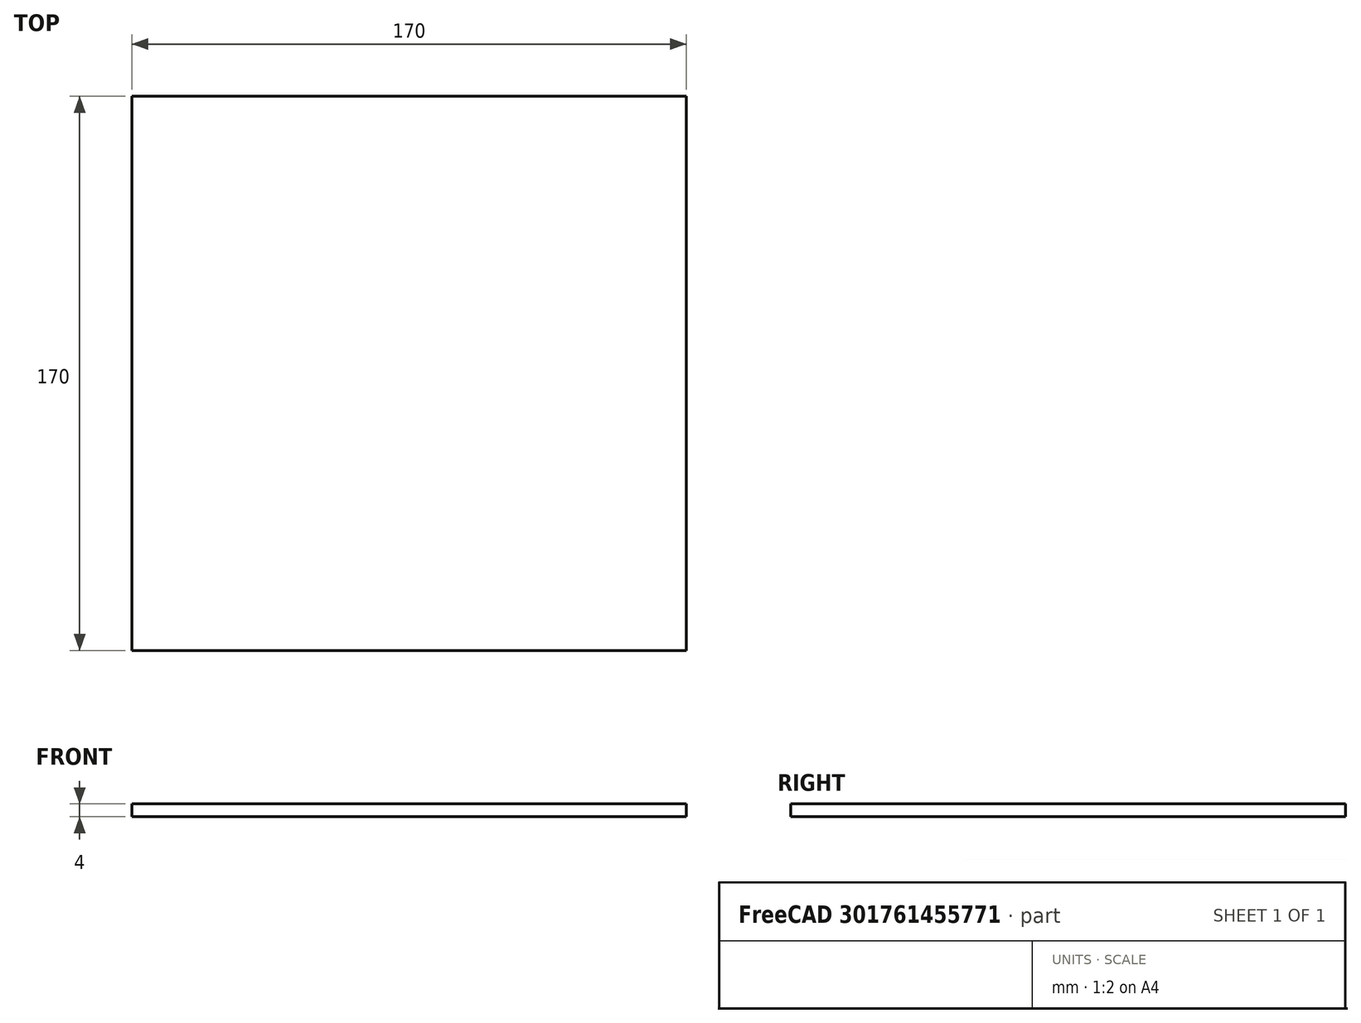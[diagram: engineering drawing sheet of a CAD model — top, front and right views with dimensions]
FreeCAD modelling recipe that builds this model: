
FCSTD DOCUMENT  (FreeCAD 1.0R39319 (Git))
Label: newAttempt
License: All rights reserved
LicenseURL: https://en.wikipedia.org/wiki/All_rights_reserved
objects: Sketcher::SketchObject×2, PartDesign::Pad×1, PartDesign::Body×1
note: 8 computed .brp shape members not serialized (recipe doc carries the construction recipe); baked Part::Feature solids carry a one-line shape summary decoded from their .brp

FEATURE [Sketcher::SketchObject] Sketch
  ArcFitTolerance = 1e-06
  AttachmentSupport = -> [XY_Plane]
  FullyConstrained = true
  MakeInternals = false
  MapMode = 5
  sketch-geometry (4):
    g0: LineSegment StartX=-85 StartY=85 StartZ=0 EndX=-85 EndY=-85 EndZ=0
    g1: LineSegment StartX=-85 StartY=-85 StartZ=0 EndX=85 EndY=-85 EndZ=0
    g2: LineSegment StartX=85 StartY=-85 StartZ=0 EndX=85 EndY=85 EndZ=0
    g3: LineSegment StartX=85 StartY=85 StartZ=0 EndX=-85 EndY=85 EndZ=0
  constraints (12):
    c: Coincident(g0,g1)
    c: Coincident(g1,g2)
    c: Coincident(g2,g3)
    c: Coincident(g3,g0)
    c: Vertical(g0)
    c: Vertical(g2)
    c: Horizontal(g1)
    c: Horizontal(g3)
    c: Distance(g0,g2) = 170
    c: Distance(g1,g3) = 170
    c: Distance(g-1,g3) = 85
    c: Distance(g0,g-2) = 85
FEATURE [PartDesign::Pad] Pad
  Direction = (0,0,1)
  Length = 4
  Length2 = 10
  Profile = -> Sketch
  ReferenceAxis = -> Sketch [N_Axis]
  Refine = true
  Suppressed = false
  Type = 0
FEATURE [Sketcher::SketchObject] Sketch001
  ArcFitTolerance = 1e-06
  AttachmentSupport = -> [Pad]
  FullyConstrained = false
  MakeInternals = false
  MapMode = 5
  Placement = pos=(0,0,4) rot=(0,0,1;0rad)
  sketch-geometry (96):
    g0: LineSegment StartX=-68.03 StartY=63 StartZ=0 EndX=-68.03 EndY=60.51 EndZ=0
    g1: LineSegment StartX=-68.03 StartY=60.51 StartZ=0 EndX=-57.97 EndY=60.51 EndZ=0
    g2: LineSegment StartX=-57.97 StartY=60.51 StartZ=0 EndX=-57.97 EndY=65.54 EndZ=0
    g3: LineSegment StartX=-57.97 StartY=65.54 StartZ=0 EndX=-63 EndY=65.54 EndZ=0
    g4: LineSegment StartX=-63 StartY=65.54 StartZ=0 EndX=-63 EndY=63 EndZ=0
    g5: LineSegment StartX=-63 StartY=63 StartZ=0 EndX=-68.03 EndY=63 EndZ=0
    g6: LineSegment StartX=-26.03 StartY=63 StartZ=0 EndX=-26.03 EndY=60.51 EndZ=0
    g7: LineSegment StartX=-26.03 StartY=60.51 StartZ=0 EndX=-15.97 EndY=60.51 EndZ=0
    g8: LineSegment StartX=-15.97 StartY=60.51 StartZ=0 EndX=-15.97 EndY=65.54 EndZ=0
    g9: LineSegment StartX=-15.97 StartY=65.54 StartZ=0 EndX=-21 EndY=65.54 EndZ=0
    g10: LineSegment StartX=-21 StartY=65.54 StartZ=0 EndX=-21 EndY=63 EndZ=0
    g11: LineSegment StartX=-21 StartY=63 StartZ=0 EndX=-26.03 EndY=63 EndZ=0
    g12: LineSegment StartX=15.97 StartY=63 StartZ=0 EndX=15.97 EndY=60.51 EndZ=0
    g13: LineSegment StartX=15.97 StartY=60.51 StartZ=0 EndX=26.03 EndY=60.51 EndZ=0
    g14: LineSegment StartX=26.03 StartY=60.51 StartZ=0 EndX=26.03 EndY=65.54 EndZ=0
    g15: LineSegment StartX=26.03 StartY=65.54 StartZ=0 EndX=21 EndY=65.54 EndZ=0
    g16: LineSegment StartX=21 StartY=65.54 StartZ=0 EndX=21 EndY=63 EndZ=0
    g17: LineSegment StartX=21 StartY=63 StartZ=0 EndX=15.97 EndY=63 EndZ=0
    g18: LineSegment StartX=57.97 StartY=63 StartZ=0 EndX=57.97 EndY=60.51 EndZ=0
    g19: LineSegment StartX=57.97 StartY=60.51 StartZ=0 EndX=68.03 EndY=60.51 EndZ=0
    g20: LineSegment StartX=68.03 StartY=60.51 StartZ=0 EndX=68.03 EndY=65.54 EndZ=0
    g21: LineSegment StartX=68.03 StartY=65.54 StartZ=0 EndX=63 EndY=65.54 EndZ=0
    g22: LineSegment StartX=63 StartY=65.54 StartZ=0 EndX=63 EndY=63 EndZ=0
    g23: LineSegment StartX=63 StartY=63 StartZ=0 EndX=57.97 EndY=63 EndZ=0
    g24: LineSegment StartX=-68.03 StartY=21 StartZ=0 EndX=-68.03 EndY=18.51 EndZ=0
    g25: LineSegment StartX=-68.03 StartY=18.51 StartZ=0 EndX=-57.97 EndY=18.51 EndZ=0
    g26: LineSegment StartX=-57.97 StartY=18.51 StartZ=0 EndX=-57.97 EndY=23.54 EndZ=0
    g27: LineSegment StartX=-57.97 StartY=23.54 StartZ=0 EndX=-63 EndY=23.54 EndZ=0
    g28: LineSegment StartX=-63 StartY=23.54 StartZ=0 EndX=-63 EndY=21 EndZ=0
    g29: LineSegment StartX=-63 StartY=21 StartZ=0 EndX=-68.03 EndY=21 EndZ=0
    g30: LineSegment StartX=-26.03 StartY=21 StartZ=0 EndX=-26.03 EndY=18.51 EndZ=0
    g31: LineSegment StartX=-26.03 StartY=18.51 StartZ=0 EndX=-15.97 EndY=18.51 EndZ=0
    g32: LineSegment StartX=-15.97 StartY=18.51 StartZ=0 EndX=-15.97 EndY=23.54 EndZ=0
    g33: LineSegment StartX=-15.97 StartY=23.54 StartZ=0 EndX=-21 EndY=23.54 EndZ=0
    g34: LineSegment StartX=-21 StartY=23.54 StartZ=0 EndX=-21 EndY=21 EndZ=0
    g35: LineSegment StartX=-21 StartY=21 StartZ=0 EndX=-26.03 EndY=21 EndZ=0
    g36: LineSegment StartX=15.97 StartY=21 StartZ=0 EndX=15.97 EndY=18.51 EndZ=0
    g37: LineSegment StartX=15.97 StartY=18.51 StartZ=0 EndX=26.03 EndY=18.51 EndZ=0
    g38: LineSegment StartX=26.03 StartY=18.51 StartZ=0 EndX=26.03 EndY=23.54 EndZ=0
    g39: LineSegment StartX=26.03 StartY=23.54 StartZ=0 EndX=21 EndY=23.54 EndZ=0
    g40: LineSegment StartX=21 StartY=23.54 StartZ=0 EndX=21 EndY=21 EndZ=0
    g41: LineSegment StartX=21 StartY=21 StartZ=0 EndX=15.97 EndY=21 EndZ=0
    g42: LineSegment StartX=57.97 StartY=21 StartZ=0 EndX=57.97 EndY=18.51 EndZ=0
    g43: LineSegment StartX=57.97 StartY=18.51 StartZ=0 EndX=68.03 EndY=18.51 EndZ=0
    g44: LineSegment StartX=68.03 StartY=18.51 StartZ=0 EndX=68.03 EndY=23.54 EndZ=0
    g45: LineSegment StartX=68.03 StartY=23.54 StartZ=0 EndX=63 EndY=23.54 EndZ=0
    g46: LineSegment StartX=63 StartY=23.54 StartZ=0 EndX=63 EndY=21 EndZ=0
    g47: LineSegment StartX=63 StartY=21 StartZ=0 EndX=57.97 EndY=21 EndZ=0
    g48: LineSegment StartX=-68.03 StartY=-21 StartZ=0 EndX=-68.03 EndY=-23.49 EndZ=0
    g49: LineSegment StartX=-68.03 StartY=-23.49 StartZ=0 EndX=-57.97 EndY=-23.49 EndZ=0
    g50: LineSegment StartX=-57.97 StartY=-23.49 StartZ=0 EndX=-57.97 EndY=-18.46 EndZ=0
    g51: LineSegment StartX=-57.97 StartY=-18.46 StartZ=0 EndX=-63 EndY=-18.46 EndZ=0
    g52: LineSegment StartX=-63 StartY=-18.46 StartZ=0 EndX=-63 EndY=-21 EndZ=0
    g53: LineSegment StartX=-63 StartY=-21 StartZ=0 EndX=-68.03 EndY=-21 EndZ=0
    g54: LineSegment StartX=-26.03 StartY=-21 StartZ=0 EndX=-26.03 EndY=-23.49 EndZ=0
    g55: LineSegment StartX=-26.03 StartY=-23.49 StartZ=0 EndX=-15.97 EndY=-23.49 EndZ=0
    g56: LineSegment StartX=-15.97 StartY=-23.49 StartZ=0 EndX=-15.97 EndY=-18.46 EndZ=0
    g57: LineSegment StartX=-15.97 StartY=-18.46 StartZ=0 EndX=-21 EndY=-18.46 EndZ=0
    g58: LineSegment StartX=-21 StartY=-18.46 StartZ=0 EndX=-21 EndY=-21 EndZ=0
    g59: LineSegment StartX=-21 StartY=-21 StartZ=0 EndX=-26.03 EndY=-21 EndZ=0
    g60: LineSegment StartX=15.97 StartY=-21 StartZ=0 EndX=15.97 EndY=-23.49 EndZ=0
    g61: LineSegment StartX=15.97 StartY=-23.49 StartZ=0 EndX=26.03 EndY=-23.49 EndZ=0
    g62: LineSegment StartX=26.03 StartY=-23.49 StartZ=0 EndX=26.03 EndY=-18.46 EndZ=0
    g63: LineSegment StartX=26.03 StartY=-18.46 StartZ=0 EndX=21 EndY=-18.46 EndZ=0
    g64: LineSegment StartX=21 StartY=-18.46 StartZ=0 EndX=21 EndY=-21 EndZ=0
    g65: LineSegment StartX=21 StartY=-21 StartZ=0 EndX=15.97 EndY=-21 EndZ=0
    g66: LineSegment StartX=57.97 StartY=-21 StartZ=0 EndX=57.97 EndY=-23.49 EndZ=0
    g67: LineSegment StartX=57.97 StartY=-23.49 StartZ=0 EndX=68.03 EndY=-23.49 EndZ=0
    g68: LineSegment StartX=68.03 StartY=-23.49 StartZ=0 EndX=68.03 EndY=-18.46 EndZ=0
    g69: LineSegment StartX=68.03 StartY=-18.46 StartZ=0 EndX=63 EndY=-18.46 EndZ=0
    g70: LineSegment StartX=63 StartY=-18.46 StartZ=0 EndX=63 EndY=-21 EndZ=0
    g71: LineSegment StartX=63 StartY=-21 StartZ=0 EndX=57.97 EndY=-21 EndZ=0
    g72: LineSegment StartX=-68.03 StartY=-63 StartZ=0 EndX=-68.03 EndY=-65.49 EndZ=0
    g73: LineSegment StartX=-68.03 StartY=-65.49 StartZ=0 EndX=-57.97 EndY=-65.49 EndZ=0
    g74: LineSegment StartX=-57.97 StartY=-65.49 StartZ=0 EndX=-57.97 EndY=-60.46 EndZ=0
    g75: LineSegment StartX=-57.97 StartY=-60.46 StartZ=0 EndX=-63 EndY=-60.46 EndZ=0
    g76: LineSegment StartX=-63 StartY=-60.46 StartZ=0 EndX=-63 EndY=-63 EndZ=0
    g77: LineSegment StartX=-63 StartY=-63 StartZ=0 EndX=-68.03 EndY=-63 EndZ=0
    g78: LineSegment StartX=-26.03 StartY=-63 StartZ=0 EndX=-26.03 EndY=-65.49 EndZ=0
    g79: LineSegment StartX=-26.03 StartY=-65.49 StartZ=0 EndX=-15.97 EndY=-65.49 EndZ=0
    g80: LineSegment StartX=-15.97 StartY=-65.49 StartZ=0 EndX=-15.97 EndY=-60.46 EndZ=0
    g81: LineSegment StartX=-15.97 StartY=-60.46 StartZ=0 EndX=-21 EndY=-60.46 EndZ=0
    g82: LineSegment StartX=-21 StartY=-60.46 StartZ=0 EndX=-21 EndY=-63 EndZ=0
    g83: LineSegment StartX=-21 StartY=-63 StartZ=0 EndX=-26.03 EndY=-63 EndZ=0
    g84: LineSegment StartX=15.97 StartY=-63 StartZ=0 EndX=15.97 EndY=-65.49 EndZ=0
    g85: LineSegment StartX=15.97 StartY=-65.49 StartZ=0 EndX=26.03 EndY=-65.49 EndZ=0
    g86: LineSegment StartX=26.03 StartY=-65.49 StartZ=0 EndX=26.03 EndY=-60.46 EndZ=0
    g87: LineSegment StartX=26.03 StartY=-60.46 StartZ=0 EndX=21 EndY=-60.46 EndZ=0
    g88: LineSegment StartX=21 StartY=-60.46 StartZ=0 EndX=21 EndY=-63 EndZ=0
    g89: LineSegment StartX=21 StartY=-63 StartZ=0 EndX=15.97 EndY=-63 EndZ=0
    g90: LineSegment StartX=57.97 StartY=-63 StartZ=0 EndX=57.97 EndY=-65.49 EndZ=0
    g91: LineSegment StartX=57.97 StartY=-65.49 StartZ=0 EndX=68.03 EndY=-65.49 EndZ=0
    g92: LineSegment StartX=68.03 StartY=-65.49 StartZ=0 EndX=68.03 EndY=-60.46 EndZ=0
    g93: LineSegment StartX=68.03 StartY=-60.46 StartZ=0 EndX=63 EndY=-60.46 EndZ=0
    g94: LineSegment StartX=63 StartY=-60.46 StartZ=0 EndX=63 EndY=-63 EndZ=0
    g95: LineSegment StartX=63 StartY=-63 StartZ=0 EndX=57.97 EndY=-63 EndZ=0
  constraints (268):
    c: Vertical(g0)
    c: Coincident(g0,g1)
    c: Horizontal(g1)
    c: Coincident(g1,g2)
    c: Vertical(g2)
    c: Coincident(g2,g3)
    c: Horizontal(g3)
    c: Coincident(g3,g4)
    c: Vertical(g4)
    c: Coincident(g4,g5)
    c: Coincident(g5,g0)
    c: Perpendicular(g4,g5)
    c: DistanceX(g3,g3) = 5.03
    c: Equal(g3,g5)
    c: Equal(g3,g2)
    c: DistanceY(g0,g0) = 2.49
    c: Distance(g4,g-2) = 63
    c: Distance(g4,g-1) = 63
    c: Vertical(g6)
    c: Vertical(g12)
    c: Vertical(g18)
    c: Vertical(g24)
    c: Vertical(g30)
    c: Vertical(g36)
    c: Vertical(g42)
    c: Vertical(g48)
    c: Vertical(g54)
    c: Vertical(g60)
    c: Vertical(g66)
    c: Vertical(g72)
    c: Vertical(g78)
    c: Vertical(g84)
    c: Vertical(g90)
    c: Coincident(g6,g7)
    c: Coincident(g12,g13)
    c: Coincident(g18,g19)
    c: Coincident(g24,g25)
    c: Coincident(g30,g31)
    c: Coincident(g36,g37)
    c: Coincident(g42,g43)
    c: Coincident(g48,g49)
    c: Coincident(g54,g55)
    c: Coincident(g60,g61)
    c: Coincident(g66,g67)
    c: Coincident(g72,g73)
    c: Coincident(g78,g79)
    c: Coincident(g84,g85)
    c: Coincident(g90,g91)
    c: Horizontal(g7)
    c: Horizontal(g13)
    c: Horizontal(g19)
    c: Horizontal(g25)
    c: Horizontal(g31)
    c: Horizontal(g37)
    c: Horizontal(g43)
    c: Horizontal(g49)
    c: Horizontal(g55)
    c: Horizontal(g61)
    c: Horizontal(g67)
    c: Horizontal(g73)
    c: Horizontal(g79)
    c: Horizontal(g85)
    c: Horizontal(g91)
    c: Coincident(g7,g8)
    c: Coincident(g13,g14)
    c: Coincident(g19,g20)
    c: Coincident(g25,g26)
    c: Coincident(g31,g32)
    c: Coincident(g37,g38)
    c: Coincident(g43,g44)
    c: Coincident(g49,g50)
    c: Coincident(g55,g56)
    c: Coincident(g61,g62)
    c: Coincident(g67,g68)
    c: Coincident(g73,g74)
    c: Coincident(g79,g80)
    c: Coincident(g85,g86)
    c: Coincident(g91,g92)
    c: Vertical(g8)
    c: Vertical(g14)
    c: Vertical(g20)
    c: Vertical(g26)
    c: Vertical(g32)
    c: Vertical(g38)
    c: Vertical(g44)
    c: Vertical(g50)
    c: Vertical(g56)
    c: Vertical(g62)
    c: Vertical(g68)
    c: Vertical(g74)
    c: Vertical(g80)
    c: Vertical(g86)
    c: Vertical(g92)
    c: Coincident(g8,g9)
    c: Coincident(g14,g15)
    c: Coincident(g20,g21)
    c: Coincident(g26,g27)
    c: Coincident(g32,g33)
    c: Coincident(g38,g39)
    c: Coincident(g44,g45)
    c: Coincident(g50,g51)
    c: Coincident(g56,g57)
    c: Coincident(g62,g63)
    c: Coincident(g68,g69)
    c: Coincident(g74,g75)
    c: Coincident(g80,g81)
    c: Coincident(g86,g87)
    c: Coincident(g92,g93)
    c: Horizontal(g9)
    c: Horizontal(g15)
    c: Horizontal(g21)
    c: Horizontal(g27)
    c: Horizontal(g33)
    c: Horizontal(g39)
    c: Horizontal(g45)
    c: Horizontal(g51)
    c: Horizontal(g57)
    c: Horizontal(g63)
    c: Horizontal(g69)
    c: Horizontal(g75)
    c: Horizontal(g81)
    c: Horizontal(g87)
    c: Horizontal(g93)
    c: Coincident(g9,g10)
    c: Coincident(g15,g16)
    c: Coincident(g21,g22)
    c: Coincident(g27,g28)
    c: Coincident(g33,g34)
    c: Coincident(g39,g40)
    c: Coincident(g45,g46)
    c: Coincident(g51,g52)
    c: Coincident(g57,g58)
    c: Coincident(g63,g64)
    c: Coincident(g69,g70)
    c: Coincident(g75,g76)
    c: Coincident(g81,g82)
    c: Coincident(g87,g88)
    c: Coincident(g93,g94)
    c: Vertical(g10)
    c: Vertical(g16)
    c: Vertical(g22)
    c: Vertical(g28)
    c: Vertical(g34)
    c: Vertical(g40)
    c: Vertical(g46)
    c: Vertical(g52)
    c: Vertical(g58)
    c: Vertical(g64)
    c: Vertical(g70)
    c: Vertical(g76)
    c: Vertical(g82)
    c: Vertical(g88)
    c: Vertical(g94)
    c: Coincident(g10,g11)
    c: Coincident(g16,g17)
    c: Coincident(g22,g23)
    c: Coincident(g28,g29)
    c: Coincident(g34,g35)
    c: Coincident(g40,g41)
    c: Coincident(g46,g47)
    c: Coincident(g52,g53)
    c: Coincident(g58,g59)
    c: Coincident(g64,g65)
    c: Coincident(g70,g71)
    c: Coincident(g76,g77)
    c: Coincident(g82,g83)
    c: Coincident(g88,g89)
    c: Coincident(g94,g95)
    c: Coincident(g11,g6)
    c: Coincident(g17,g12)
    c: Coincident(g23,g18)
    c: Coincident(g29,g24)
    c: Coincident(g35,g30)
    c: Coincident(g41,g36)
    c: Coincident(g47,g42)
    c: Coincident(g53,g48)
    c: Coincident(g59,g54)
    c: Coincident(g65,g60)
    c: Coincident(g71,g66)
    c: Coincident(g77,g72)
    c: Coincident(g83,g78)
    c: Coincident(g89,g84)
    c: Coincident(g95,g90)
    c: Perpendicular(g10,g11)
    c: Perpendicular(g16,g17)
    c: Perpendicular(g22,g23)
    c: Perpendicular(g28,g29)
    c: Perpendicular(g34,g35)
    c: Perpendicular(g40,g41)
    c: Perpendicular(g46,g47)
    c: Perpendicular(g52,g53)
    c: Perpendicular(g58,g59)
    c: Perpendicular(g64,g65)
    c: Perpendicular(g70,g71)
    c: Perpendicular(g76,g77)
    c: Perpendicular(g82,g83)
    c: Perpendicular(g88,g89)
    c: Perpendicular(g94,g95)
    c: Equal(g3,g9)
    c: Equal(g3,g15)
    c: Equal(g3,g21)
    c: Equal(g3,g27)
    c: Equal(g3,g33)
    c: Equal(g3,g39)
    c: Equal(g3,g45)
    c: Equal(g3,g51)
    c: Equal(g3,g57)
    c: Equal(g3,g63)
    c: Equal(g3,g69)
    c: Equal(g3,g75)
    c: Equal(g3,g81)
    c: Equal(g3,g87)
    c: Equal(g3,g93)
    c: Equal(g9,g11)
    c: Equal(g15,g17)
    c: Equal(g21,g23)
    c: Equal(g27,g29)
    c: Equal(g33,g35)
    c: Equal(g39,g41)
    c: Equal(g45,g47)
    c: Equal(g51,g53)
    c: Equal(g57,g59)
    c: Equal(g63,g65)
    c: Equal(g69,g71)
    c: Equal(g75,g77)
    c: Equal(g81,g83)
    c: Equal(g87,g89)
    c: Equal(g93,g95)
    c: Equal(g9,g8)
    c: Equal(g15,g14)
    c: Equal(g21,g20)
    c: Equal(g27,g26)
    c: Equal(g33,g32)
    c: Equal(g39,g38)
    c: Equal(g45,g44)
    c: Equal(g51,g50)
    c: Equal(g57,g56)
    c: Equal(g63,g62)
    c: Equal(g69,g68)
    c: Equal(g75,g74)
    c: Equal(g81,g80)
    c: Equal(g87,g86)
    c: Equal(g93,g92)
    c: Equal(g0,g6)
    c: Equal(g0,g12)
    c: Equal(g0,g18)
    c: Equal(g0,g24)
    c: Equal(g0,g30)
    c: Equal(g0,g36)
    c: Equal(g0,g42)
    c: Equal(g0,g48)
    c: Equal(g0,g54)
    c: Equal(g0,g60)
    c: Equal(g0,g66)
    c: Equal(g0,g72)
    c: Equal(g0,g78)
    c: Equal(g0,g84)
    c: Equal(g0,g90)
    c: Distance(g10,g-2) = 21
    c: Distance(g16,g-2) = 21
    c: Distance(g22,g-2) = 63
    c: Distance(g28,g-1) = 21
    c: Distance(g34,g-1) = 21
    c: Distance(g40,g-1) = 21
    c: Distance(g40,g-2) = 21
    c: Distance(g34,g-2) = 21
    c: Distance(g28,g-2) = 63
    c: Distance(g46,g-2) = 63
FEATURE [PartDesign::Body] Body
  AllowCompound = false
  Group = -> [Sketch,Pad,Sketch001]
  Origin = -> Origin
  Tip = -> Pad
